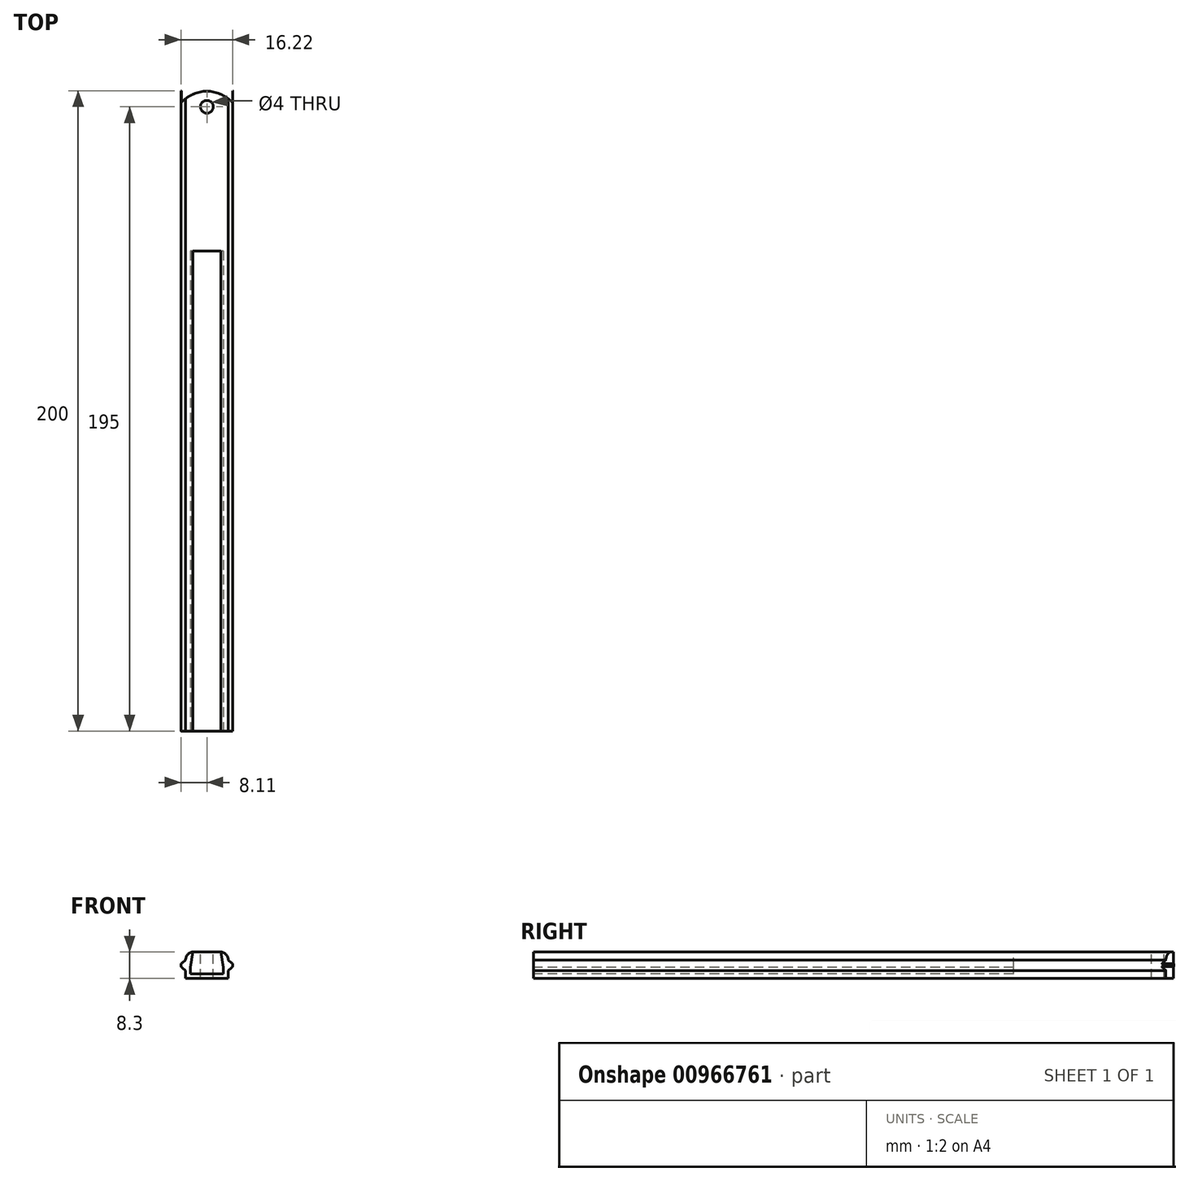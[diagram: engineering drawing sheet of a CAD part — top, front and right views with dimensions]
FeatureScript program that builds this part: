
annotation { "Feature Type Name" : "Feature", "Feature Type Description" : "" }
export const myFeature = defineFeature(function(context is Context, id is Id, definition is map)
    precondition{}
    {
        {
            var Q0;
            Q0=qCreatedBy(makeId("Front.planeOp"),FACE);
            var sketch = newSketch(context, id + "F0", { "sketchPlane" : qUnion([Q0])});
            skLineSegment(sketch, "E0.bottom", {"start": v(4.15, -2.65) * mm, "end": v(-4.15, -2.65) * mm});
            skLineSegment(sketch, "E0.top", {"start": v(4.15, 2.65) * mm, "end": v(-4.15, 2.65) * mm});
            skLineSegment(sketch, "E0.left", {"start": v(5.15, -1.65) * mm, "end": v(5.15, 1.65) * mm});
            skLineSegment(sketch, "E0.right", {"start": v(-5.15, -1.65) * mm, "end": v(-5.15, 1.65) * mm});
            skPoint(sketch, "E0.middle", {"position": v(0, 0) * mm});
            skPoint(sketch, "E1.visualSharp", {"position": v(-5.15, 2.65) * mm});
            skArc(sketch, "E1.filletArc", {"start": v(-4.15, 2.65) * mm, "mid": v(-4.86, 2.36) * mm, "end": v(-5.15, 1.65) * mm});
            skPoint(sketch, "E2.visualSharp", {"position": v(5.15, 2.65) * mm});
            skArc(sketch, "E2.filletArc", {"start": v(5.15, 1.65) * mm, "mid": v(4.86, 2.36) * mm, "end": v(4.15, 2.65) * mm});
            skPoint(sketch, "E3.visualSharp", {"position": v(5.15, -2.65) * mm});
            skArc(sketch, "E3.filletArc", {"start": v(4.15, -2.65) * mm, "mid": v(4.86, -2.36) * mm, "end": v(5.15, -1.65) * mm});
            skPoint(sketch, "E4.visualSharp", {"position": v(-5.15, -2.65) * mm});
            skArc(sketch, "E4.filletArc", {"start": v(-5.15, -1.65) * mm, "mid": v(-4.86, -2.36) * mm, "end": v(-4.15, -2.65) * mm});
            skArc(sketch, "E5.0", {"start": v(6.65, 1.65) * mm, "mid": v(5.92, 3.42) * mm, "end": v(4.15, 4.15) * mm});
            skLineSegment(sketch, "E5.2", {"start": v(4.15, 4.15) * mm, "end": v(-4.15, 4.15) * mm});
            skArc(sketch, "E5.4", {"start": v(-4.15, 4.15) * mm, "mid": v(-5.92, 3.42) * mm, "end": v(-6.65, 1.65) * mm});
            skLineSegment(sketch, "E5.7", {"start": v(4.15, -4.15) * mm, "end": v(-4.15, -4.15) * mm});
            skLineSegment(sketch, "E6", {"start": v(-7.73, 0.78) * mm, "end": v(-6.65, 1.65) * mm});
            skLineSegment(sketch, "E7.MirrorCS", {"start": v(-7.73, -0.78) * mm, "end": v(-6.65, -1.65) * mm});
            skLineSegment(sketch, "E8.MirrorCS", {"start": v(7.73, 0.78) * mm, "end": v(6.65, 1.65) * mm});
            skLineSegment(sketch, "E9.MirrorCS", {"start": v(7.73, -0.78) * mm, "end": v(6.65, -1.65) * mm});
            skPoint(sketch, "E10.visualSharp", {"position": v(-8.7, 0) * mm});
            skArc(sketch, "E10.filletArc", {"start": v(-7.73, 0.78) * mm, "mid": v(-8.1, 0) * mm, "end": v(-7.73, -0.78) * mm});
            skPoint(sketch, "E11.visualSharp", {"position": v(8.7, 0) * mm});
            skArc(sketch, "E11.filletArc", {"start": v(7.73, -0.78) * mm, "mid": v(8.1, 0) * mm, "end": v(7.73, 0.78) * mm});
            skLineSegment(sketch, "E12", {"start": v(-4.15, -4.15) * mm, "end": v(-6.65, -4.15) * mm});
            skLineSegment(sketch, "E13", {"start": v(-6.65, -4.15) * mm, "end": v(-6.65, -1.65) * mm});
            skLineSegment(sketch, "E14", {"start": v(4.15, -4.15) * mm, "end": v(6.65, -4.15) * mm});
            skLineSegment(sketch, "E15", {"start": v(6.65, -4.15) * mm, "end": v(6.65, -1.65) * mm});
            skSolve(sketch);
        }
        {
            var Q0;
            Q0=makeQuery(id+"F0.imprint","IMPRINT",FACE,{"disambiguationData":[TD([[makeQuery(id+"F0.imprint","IMPRINT",EDGE,{"derivedFrom":sQuery(id+"F0.wireOp",EDGE,"E0.bottom")}),1.0]])]});
            var Q1;
            Q1=makeQuery(id+"F0.imprint","IMPRINT",FACE,{"disambiguationData":[TD([[makeQuery(id+"F0.imprint","IMPRINT",EDGE,{"derivedFrom":sQuery(id+"F0.wireOp",EDGE,"E0.bottom")}),-1.0]])]});
            extrude(context, id + "F1", {"entities" : qUnion([Q0, Q1]), "depth" : 200 * mm, "offsetDistance" : 25 * mm});
        }
        {
            var Q0;
            Q0=makeQuery(id+"F1.opExtrude","SWEPT_FACE",FACE,{"disambiguationData":[OSD([sQuery(id+"F0.wireOp",EDGE,"E5.2")])]});
            var sketch = newSketch(context, id + "F2", { "sketchPlane" : qUnion([Q0])});
            skCircle(sketch, "E16", {"center": v(0, -5) * mm, "radius": 2 * mm});
            skSolve(sketch);
        }
        {
            var Q0;
            Q0=makeQuery(id+"F2.imprint","IMPRINT",FACE,{"disambiguationData":[TD([[makeQuery(id+"F2.imprint","IMPRINT",EDGE,{"derivedFrom":sQuery(id+"F2.wireOp",EDGE,"S33YdpTx-NKYe-flyp-kQUo-xBa4HNO2xXOk")}),1.0]])]});
            var Q1;
            Q1=makeQuery(id+"F2.imprint","IMPRINT",FACE,{"disambiguationData":[TD([[makeQuery(id+"F2.imprint","IMPRINT",EDGE,{"derivedFrom":sQuery(id+"F2.wireOp",EDGE,"E16")}),1.0]])]});
            extrude(context, id + "F3", {"entities" : qUnion([Q0, Q1]), "operationType" : NewBodyOperationType.REMOVE, "endBound" : BoundingType.THROUGH_ALL, "oppositeDirection" : true, "depth" : 25 * mm, "offsetDistance" : 25 * mm});
        }
        {
            var Q0;
            Q0=qCreatedBy(makeId("Top.planeOp"),FACE);
            cPlane(context, id + "F4", {"entities" : qUnion([Q0]), "cplaneType" : CPlaneType.OFFSET, "offset" : 4.6 * mm, "width" : 150 * mm, "height" : 150 * mm});
        }
        {
            var Q0;
            Q0=qCreatedBy(id+"F4.planeOp",FACE);
            var sketch = newSketch(context, id + "F5", { "sketchPlane" : qUnion([Q0])});
            skLineSegment(sketch, "E17.bottom", {"start": v(8, 3.7) * mm, "end": v(-8, 3.7) * mm});
            skLineSegment(sketch, "E17.left", {"start": v(8, 3.7) * mm, "end": v(8, -3.7) * mm});
            skLineSegment(sketch, "E17.right", {"start": v(-8, 3.7) * mm, "end": v(-8, -3.7) * mm});
            skPoint(sketch, "E17.middle", {"position": v(0, 0) * mm});
            skArc(sketch, "E18", {"start": v(8, -3.7) * mm, "mid": v(0, -0.15) * mm, "end": v(-8, -3.7) * mm});
            skSolve(sketch);
        }
        {
            var Q0;
            Q0=makeQuery(id+"F5.imprint","IMPRINT",FACE,{"disambiguationData":[TD([[makeQuery(id+"F5.imprint","IMPRINT",EDGE,{"derivedFrom":sQuery(id+"F5.wireOp",EDGE,"E17.bottom")}),1.0]])]});
            extrude(context, id + "F6", {"entities" : qUnion([Q0]), "operationType" : NewBodyOperationType.REMOVE, "oppositeDirection" : true, "depth" : 25 * mm, "offsetDistance" : 25 * mm});
        }
        {
            var Q0;
            Q0=makeQuery(id+"F1.opExtrude","CAP_FACE",FACE,{"disambiguationData":[OSD([sQuery(id+"F0.wireOp",EDGE,"E0.bottom"),sQuery(id+"F0.wireOp",EDGE,"E0.top"),sQuery(id+"F0.wireOp",EDGE,"E0.left"),sQuery(id+"F0.wireOp",EDGE,"E0.right"),sQuery(id+"F0.wireOp",EDGE,"E1.filletArc"),sQuery(id+"F0.wireOp",EDGE,"E2.filletArc"),sQuery(id+"F0.wireOp",EDGE,"E3.filletArc"),sQuery(id+"F0.wireOp",EDGE,"E4.filletArc"),sQuery(id+"F0.wireOp",EDGE,"E5.0"),sQuery(id+"F0.wireOp",EDGE,"E5.2"),sQuery(id+"F0.wireOp",EDGE,"E5.3"),sQuery(id+"F0.wireOp",EDGE,"E5.4"),sQuery(id+"F0.wireOp",EDGE,"E5.6"),sQuery(id+"F0.wireOp",EDGE,"E5.7"),sQuery(id+"F0.wireOp",EDGE,"E6"),sQuery(id+"F0.wireOp",EDGE,"E7.MirrorCS"),sQuery(id+"F0.wireOp",EDGE,"E8.MirrorCS"),sQuery(id+"F0.wireOp",EDGE,"E9.MirrorCS"),sQuery(id+"F0.wireOp",EDGE,"E10.filletArc"),sQuery(id+"F0.wireOp",EDGE,"E11.filletArc")])],"isStart":false});
            cPlane(context, id + "F7", {"entities" : qUnion([Q0]), "cplaneType" : CPlaneType.OFFSET, "offset" : 0 * mm, "width" : 150 * mm, "height" : 150 * mm});
        }
        {
            var Q0;
            Q0=qCreatedBy(id+"F7.planeOp",FACE);
            var sketch = newSketch(context, id + "F8", { "sketchPlane" : qUnion([Q0])});
            skLineSegment(sketch, "E19", {"start": v(0, -2.65) * mm, "end": v(5.13, -2.65) * mm});
            skLineSegment(sketch, "E20", {"start": v(5.13, -2.65) * mm, "end": v(5.13, -0.66) * mm});
            skLineSegment(sketch, "E21", {"start": v(5.13, -0.66) * mm, "end": v(4.39, 4.35) * mm});
            skLineSegment(sketch, "E22", {"start": v(4.39, 4.35) * mm, "end": v(0, 4.35) * mm});
            skLineSegment(sketch, "E23.MirrorCS", {"start": v(-4.39, 4.35) * mm, "end": v(0, 4.35) * mm});
            skLineSegment(sketch, "E24.MirrorCS", {"start": v(-5.13, -0.66) * mm, "end": v(-4.39, 4.35) * mm});
            skLineSegment(sketch, "E25.MirrorCS", {"start": v(-5.13, -2.65) * mm, "end": v(-5.13, -0.66) * mm});
            skLineSegment(sketch, "E26.MirrorCS", {"start": v(0, -2.65) * mm, "end": v(-5.13, -2.65) * mm});
            skSolve(sketch);
        }
        {
            var Q0;
            Q0=makeQuery(id+"F8.imprint","IMPRINT",FACE,{"disambiguationData":[TD([[makeQuery(id+"F8.imprint","IMPRINT",EDGE,{"derivedFrom":sQuery(id+"F8.wireOp",EDGE,"E19")}),1.0]])]});
            extrude(context, id + "F9", {"entities" : qUnion([Q0]), "operationType" : NewBodyOperationType.REMOVE, "oppositeDirection" : true, "depth" : 150 * mm, "offsetDistance" : 25 * mm});
        }
    });
